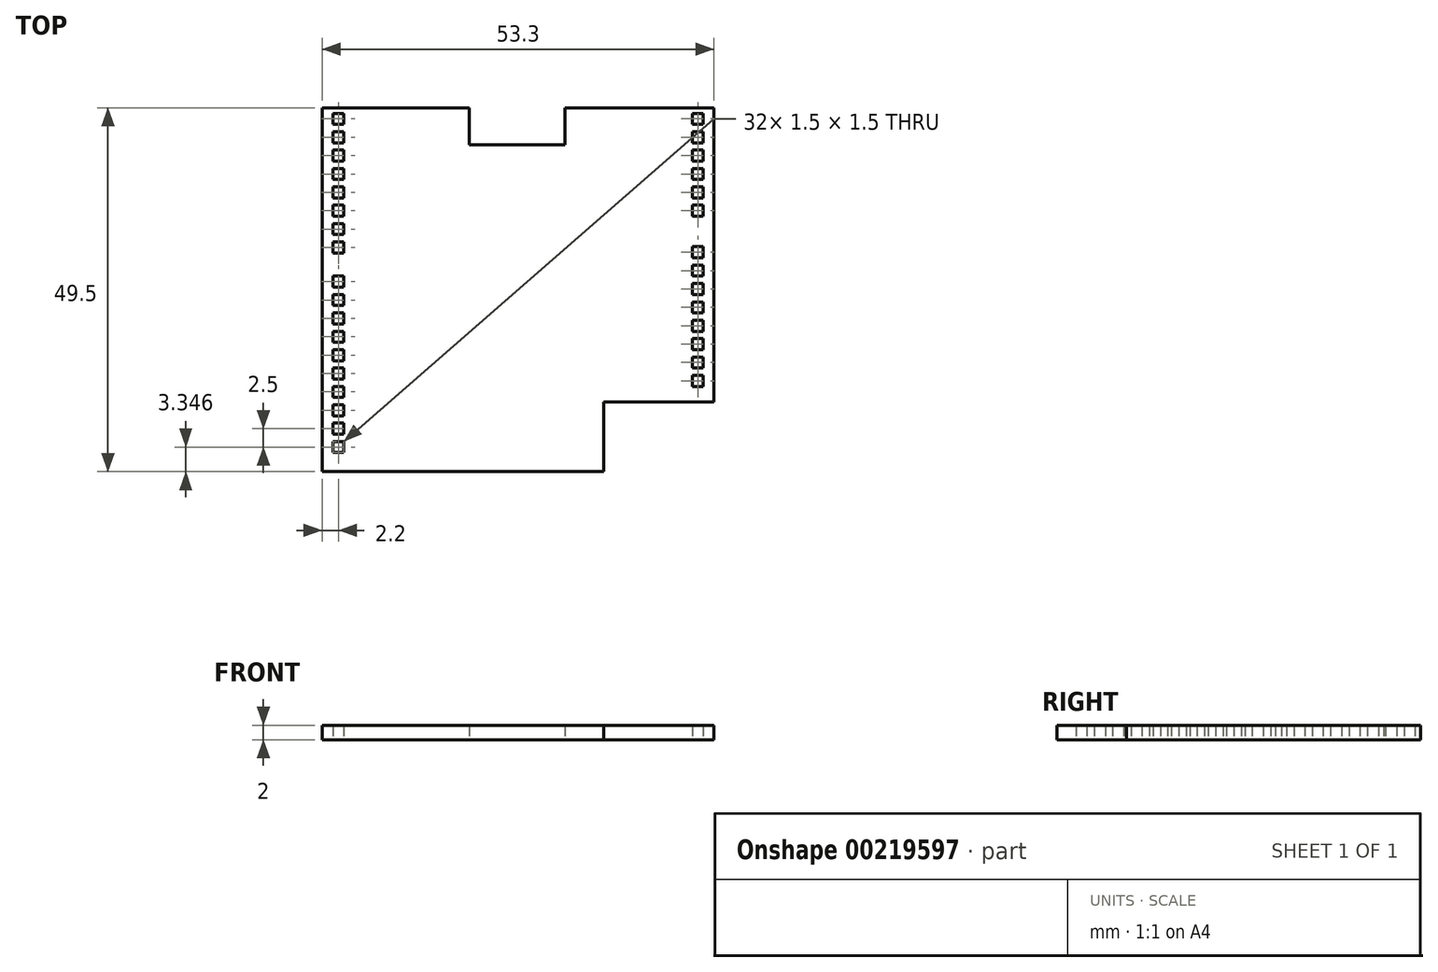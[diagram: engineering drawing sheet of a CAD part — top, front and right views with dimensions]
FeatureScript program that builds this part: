
annotation { "Feature Type Name" : "Feature", "Feature Type Description" : "" }
export const myFeature = defineFeature(function(context is Context, id is Id, definition is map)
    precondition{}
    {
        {
            var Q0;
            Q0=qCreatedBy(makeId("Top.planeOp"),FACE);
            var sketch = newSketch(context, id + "F0", { "sketchPlane" : qUnion([Q0])});
            skLineSegment(sketch, "E0.bottom", {"start": v(26.65, 29.09) * mm, "end": v(6.35, 29.09) * mm});
            skLineSegment(sketch, "E0.top", {"start": v(26.65, -29.09) * mm, "end": v(-26.65, -29.09) * mm, "construction": true});
            skLineSegment(sketch, "E0.left", {"start": v(26.65, 29.09) * mm, "end": v(26.65, -29.09) * mm});
            skLineSegment(sketch, "E0.right", {"start": v(-26.65, 29.09) * mm, "end": v(-26.65, -29.09) * mm});
            skPoint(sketch, "E0.middle", {"position": v(0, 0) * mm});
            skLineSegment(sketch, "E1.top", {"start": v(-6.65, 24.09) * mm, "end": v(6.35, 24.09) * mm});
            skLineSegment(sketch, "E1.left", {"start": v(-6.65, 29.09) * mm, "end": v(-6.65, 24.09) * mm});
            skLineSegment(sketch, "E1.right", {"start": v(6.35, 29.09) * mm, "end": v(6.35, 24.09) * mm});
            skLineSegment(sketch, "E2.bottom", {"start": v(-25.45, 29.09) * mm, "end": v(-23.45, 29.09) * mm});
            skLineSegment(sketch, "E2.top", {"start": v(-25.45, -18.91) * mm, "end": v(-23.45, -18.91) * mm, "construction": true});
            skLineSegment(sketch, "E2.left", {"start": v(-25.45, 29.09) * mm, "end": v(-25.45, 9.09) * mm, "construction": true});
            skLineSegment(sketch, "E2.right", {"start": v(-23.45, 29.09) * mm, "end": v(-23.45, 9.09) * mm, "construction": true});
            skLineSegment(sketch, "E3.bottom", {"start": v(23.45, 29.09) * mm, "end": v(25.45, 29.09) * mm});
            skLineSegment(sketch, "E3.top", {"start": v(23.45, -9.41) * mm, "end": v(25.45, -9.41) * mm, "construction": true});
            skLineSegment(sketch, "E3.left", {"start": v(23.45, 29.09) * mm, "end": v(23.45, 13.59) * mm, "construction": true});
            skLineSegment(sketch, "E3.right", {"start": v(25.45, 29.09) * mm, "end": v(25.45, 13.59) * mm, "construction": true});
            skLineSegment(sketch, "E4.bottom", {"start": v(-23.7, 26.84) * mm, "end": v(-25.2, 26.84) * mm});
            skLineSegment(sketch, "E4.top", {"start": v(-23.7, 28.34) * mm, "end": v(-25.2, 28.34) * mm});
            skLineSegment(sketch, "E4.left", {"start": v(-23.7, 26.84) * mm, "end": v(-23.7, 28.34) * mm});
            skLineSegment(sketch, "E4.right", {"start": v(-25.2, 26.84) * mm, "end": v(-25.2, 28.34) * mm});
            skPoint(sketch, "E4.middle", {"position": v(-24.45, 27.59) * mm});
            skPoint(sketch, "E4.middle.positionSnap0", {"position": v(-24.45, 29.09) * mm});
            skPoint(sketch, "E4.centerSnap0", {"position": v(-24.45, 29.09) * mm});
            skLineSegment(sketch, "E5.left", {"start": v(25.2, 26.59) * mm, "end": v(25.2, 28.09) * mm});
            skPoint(sketch, "E5.middle", {"position": v(24.45, 27.34) * mm});
            skPoint(sketch, "E5.middle.positionSnap0", {"position": v(24.45, 29.09) * mm});
            skPoint(sketch, "E5.centerSnap0", {"position": v(24.45, 29.09) * mm});
            skPoint(sketch, "E6", {"position": v(-9.25, 35.02) * mm});
            skPoint(sketch, "E7", {"position": v(18.65, 35.02) * mm});
            skLineSegment(sketch, "E8.trimOffspring", {"start": v(-6.65, 29.09) * mm, "end": v(-26.65, 29.09) * mm});
            skLineSegment(sketch, "E9", {"start": v(-26.65, -20.41) * mm, "end": v(11.65, -20.41) * mm});
            skLineSegment(sketch, "E10", {"start": v(11.65, -20.41) * mm, "end": v(11.65, -10.91) * mm});
            skLineSegment(sketch, "E11", {"start": v(11.65, -10.91) * mm, "end": v(26.65, -10.91) * mm});
            skLineSegment(sketch, "E12", {"start": v(-25.45, 9.09) * mm, "end": v(-23.45, 9.09) * mm, "construction": true});
            skLineSegment(sketch, "E13", {"start": v(-23.45, 7.09) * mm, "end": v(-25.45, 7.09) * mm, "construction": true});
            skLineSegment(sketch, "E14.trimOffspring", {"start": v(-23.45, 7.09) * mm, "end": v(-23.45, -18.91) * mm, "construction": true});
            skLineSegment(sketch, "E15.trimOffspring", {"start": v(-25.45, 7.09) * mm, "end": v(-25.45, -18.91) * mm, "construction": true});
            skLineSegment(sketch, "E16", {"start": v(23.45, 13.59) * mm, "end": v(25.45, 13.59) * mm, "construction": true});
            skLineSegment(sketch, "E17", {"start": v(25.45, 11.09) * mm, "end": v(23.45, 11.09) * mm, "construction": true});
            skLineSegment(sketch, "E18.trimOffspring", {"start": v(23.45, 11.09) * mm, "end": v(23.45, -9.41) * mm, "construction": true});
            skLineSegment(sketch, "E19.trimOffspring", {"start": v(25.45, 11.09) * mm, "end": v(25.45, -9.41) * mm, "construction": true});
            skLineSegment(sketch, "E20.0.1.0", {"start": v(-23.7, 24.34) * mm, "end": v(-23.7, 25.84) * mm});
            skPoint(sketch, "E20.0.1.1", {"position": v(-24.45, 25.09) * mm});
            skLineSegment(sketch, "E20.0.1.2", {"start": v(-23.7, 25.84) * mm, "end": v(-25.2, 25.84) * mm});
            skLineSegment(sketch, "E20.0.1.3", {"start": v(-23.7, 24.34) * mm, "end": v(-25.2, 24.34) * mm});
            skLineSegment(sketch, "E20.0.1.4", {"start": v(-25.2, 24.34) * mm, "end": v(-25.2, 25.84) * mm});
            skLineSegment(sketch, "E20.0.2.0", {"start": v(-23.7, 21.84) * mm, "end": v(-23.7, 23.34) * mm});
            skPoint(sketch, "E20.0.2.1", {"position": v(-24.45, 22.59) * mm});
            skLineSegment(sketch, "E20.0.2.2", {"start": v(-23.7, 23.34) * mm, "end": v(-25.2, 23.34) * mm});
            skLineSegment(sketch, "E20.0.2.3", {"start": v(-23.7, 21.84) * mm, "end": v(-25.2, 21.84) * mm});
            skLineSegment(sketch, "E20.0.2.4", {"start": v(-25.2, 21.84) * mm, "end": v(-25.2, 23.34) * mm});
            skLineSegment(sketch, "E20.0.3.0", {"start": v(-23.7, 19.34) * mm, "end": v(-23.7, 20.84) * mm});
            skPoint(sketch, "E20.0.3.1", {"position": v(-24.45, 20.09) * mm});
            skLineSegment(sketch, "E20.0.3.2", {"start": v(-23.7, 20.84) * mm, "end": v(-25.2, 20.84) * mm});
            skLineSegment(sketch, "E20.0.3.3", {"start": v(-23.7, 19.34) * mm, "end": v(-25.2, 19.34) * mm});
            skLineSegment(sketch, "E20.0.3.4", {"start": v(-25.2, 19.34) * mm, "end": v(-25.2, 20.84) * mm});
            skLineSegment(sketch, "E20.0.4.0", {"start": v(-23.7, 16.84) * mm, "end": v(-23.7, 18.34) * mm});
            skPoint(sketch, "E20.0.4.1", {"position": v(-24.45, 17.59) * mm});
            skLineSegment(sketch, "E20.0.4.2", {"start": v(-23.7, 18.34) * mm, "end": v(-25.2, 18.34) * mm});
            skLineSegment(sketch, "E20.0.4.3", {"start": v(-23.7, 16.84) * mm, "end": v(-25.2, 16.84) * mm});
            skLineSegment(sketch, "E20.0.4.4", {"start": v(-25.2, 16.84) * mm, "end": v(-25.2, 18.34) * mm});
            skLineSegment(sketch, "E20.0.5.0", {"start": v(-23.7, 14.34) * mm, "end": v(-23.7, 15.84) * mm});
            skPoint(sketch, "E20.0.5.1", {"position": v(-24.45, 15.09) * mm});
            skLineSegment(sketch, "E20.0.5.2", {"start": v(-23.7, 15.84) * mm, "end": v(-25.2, 15.84) * mm});
            skLineSegment(sketch, "E20.0.5.3", {"start": v(-23.7, 14.34) * mm, "end": v(-25.2, 14.34) * mm});
            skLineSegment(sketch, "E20.0.5.4", {"start": v(-25.2, 14.34) * mm, "end": v(-25.2, 15.84) * mm});
            skLineSegment(sketch, "E20.0.6.0", {"start": v(-23.7, 11.84) * mm, "end": v(-23.7, 13.34) * mm});
            skPoint(sketch, "E20.0.6.1", {"position": v(-24.45, 12.59) * mm});
            skLineSegment(sketch, "E20.0.6.2", {"start": v(-23.7, 13.34) * mm, "end": v(-25.2, 13.34) * mm});
            skLineSegment(sketch, "E20.0.6.3", {"start": v(-23.7, 11.84) * mm, "end": v(-25.2, 11.84) * mm});
            skLineSegment(sketch, "E20.0.6.4", {"start": v(-25.2, 11.84) * mm, "end": v(-25.2, 13.34) * mm});
            skLineSegment(sketch, "E20.0.7.0", {"start": v(-23.7, 9.34) * mm, "end": v(-23.7, 10.84) * mm});
            skPoint(sketch, "E20.0.7.1", {"position": v(-24.45, 10.09) * mm});
            skLineSegment(sketch, "E20.0.7.2", {"start": v(-23.7, 10.84) * mm, "end": v(-25.2, 10.84) * mm});
            skLineSegment(sketch, "E20.0.7.3", {"start": v(-23.7, 9.34) * mm, "end": v(-25.2, 9.34) * mm});
            skLineSegment(sketch, "E20.0.7.4", {"start": v(-25.2, 9.34) * mm, "end": v(-25.2, 10.84) * mm});
            skLineSegment(sketch, "E20.direction1", {"start": v(-25.2, 26.84) * mm, "end": v(-0.2, 26.84) * mm, "construction": true});
            skLineSegment(sketch, "E20.direction2", {"start": v(-25.2, 26.84) * mm, "end": v(-25.2, 24.34) * mm, "construction": true});
            skLineSegment(sketch, "E21.bottom", {"start": v(-23.7, 4.69) * mm, "end": v(-25.2, 4.69) * mm});
            skLineSegment(sketch, "E21.top", {"start": v(-23.7, 6.19) * mm, "end": v(-25.2, 6.19) * mm});
            skLineSegment(sketch, "E21.left", {"start": v(-23.7, 4.69) * mm, "end": v(-23.7, 6.19) * mm});
            skLineSegment(sketch, "E21.right", {"start": v(-25.2, 4.69) * mm, "end": v(-25.2, 6.19) * mm});
            skPoint(sketch, "E21.middle", {"position": v(-24.45, 5.44) * mm});
            skPoint(sketch, "E21.middle.positionSnap0", {"position": v(-24.45, 7.09) * mm});
            skPoint(sketch, "E21.centerSnap0", {"position": v(-24.45, 7.09) * mm});
            skLineSegment(sketch, "E22.0.1.0", {"start": v(-25.2, 2.19) * mm, "end": v(-25.2, 3.69) * mm});
            skPoint(sketch, "E22.0.1.1", {"position": v(-24.45, 2.94) * mm});
            skLineSegment(sketch, "E22.0.1.2", {"start": v(-23.7, 2.19) * mm, "end": v(-23.7, 3.69) * mm});
            skLineSegment(sketch, "E22.0.1.3", {"start": v(-23.7, 2.19) * mm, "end": v(-25.2, 2.19) * mm});
            skLineSegment(sketch, "E22.0.1.4", {"start": v(-23.7, 3.69) * mm, "end": v(-25.2, 3.69) * mm});
            skLineSegment(sketch, "E22.0.2.0", {"start": v(-25.2, -0.31) * mm, "end": v(-25.2, 1.19) * mm});
            skPoint(sketch, "E22.0.2.1", {"position": v(-24.45, 0.44) * mm});
            skLineSegment(sketch, "E22.0.2.2", {"start": v(-23.7, -0.31) * mm, "end": v(-23.7, 1.19) * mm});
            skLineSegment(sketch, "E22.0.2.3", {"start": v(-23.7, -0.31) * mm, "end": v(-25.2, -0.31) * mm});
            skLineSegment(sketch, "E22.0.2.4", {"start": v(-23.7, 1.19) * mm, "end": v(-25.2, 1.19) * mm});
            skLineSegment(sketch, "E22.0.3.0", {"start": v(-25.2, -2.81) * mm, "end": v(-25.2, -1.31) * mm});
            skPoint(sketch, "E22.0.3.1", {"position": v(-24.45, -2.06) * mm});
            skLineSegment(sketch, "E22.0.3.2", {"start": v(-23.7, -2.81) * mm, "end": v(-23.7, -1.31) * mm});
            skLineSegment(sketch, "E22.0.3.3", {"start": v(-23.7, -2.81) * mm, "end": v(-25.2, -2.81) * mm});
            skLineSegment(sketch, "E22.0.3.4", {"start": v(-23.7, -1.31) * mm, "end": v(-25.2, -1.31) * mm});
            skLineSegment(sketch, "E22.0.4.0", {"start": v(-25.2, -5.31) * mm, "end": v(-25.2, -3.81) * mm});
            skPoint(sketch, "E22.0.4.1", {"position": v(-24.45, -4.56) * mm});
            skLineSegment(sketch, "E22.0.4.2", {"start": v(-23.7, -5.31) * mm, "end": v(-23.7, -3.81) * mm});
            skLineSegment(sketch, "E22.0.4.3", {"start": v(-23.7, -5.31) * mm, "end": v(-25.2, -5.31) * mm});
            skLineSegment(sketch, "E22.0.4.4", {"start": v(-23.7, -3.81) * mm, "end": v(-25.2, -3.81) * mm});
            skLineSegment(sketch, "E22.0.5.0", {"start": v(-25.2, -7.81) * mm, "end": v(-25.2, -6.31) * mm});
            skPoint(sketch, "E22.0.5.1", {"position": v(-24.45, -7.06) * mm});
            skLineSegment(sketch, "E22.0.5.2", {"start": v(-23.7, -7.81) * mm, "end": v(-23.7, -6.31) * mm});
            skLineSegment(sketch, "E22.0.5.3", {"start": v(-23.7, -7.81) * mm, "end": v(-25.2, -7.81) * mm});
            skLineSegment(sketch, "E22.0.5.4", {"start": v(-23.7, -6.31) * mm, "end": v(-25.2, -6.31) * mm});
            skLineSegment(sketch, "E22.0.6.0", {"start": v(-25.2, -10.31) * mm, "end": v(-25.2, -8.81) * mm});
            skPoint(sketch, "E22.0.6.1", {"position": v(-24.45, -9.56) * mm});
            skLineSegment(sketch, "E22.0.6.2", {"start": v(-23.7, -10.31) * mm, "end": v(-23.7, -8.81) * mm});
            skLineSegment(sketch, "E22.0.6.3", {"start": v(-23.7, -10.31) * mm, "end": v(-25.2, -10.31) * mm});
            skLineSegment(sketch, "E22.0.6.4", {"start": v(-23.7, -8.81) * mm, "end": v(-25.2, -8.81) * mm});
            skLineSegment(sketch, "E22.0.7.0", {"start": v(-25.2, -12.81) * mm, "end": v(-25.2, -11.31) * mm});
            skPoint(sketch, "E22.0.7.1", {"position": v(-24.45, -12.06) * mm});
            skLineSegment(sketch, "E22.0.7.2", {"start": v(-23.7, -12.81) * mm, "end": v(-23.7, -11.31) * mm});
            skLineSegment(sketch, "E22.0.7.3", {"start": v(-23.7, -12.81) * mm, "end": v(-25.2, -12.81) * mm});
            skLineSegment(sketch, "E22.0.7.4", {"start": v(-23.7, -11.31) * mm, "end": v(-25.2, -11.31) * mm});
            skLineSegment(sketch, "E22.0.8.0", {"start": v(-25.2, -15.31) * mm, "end": v(-25.2, -13.81) * mm});
            skPoint(sketch, "E22.0.8.1", {"position": v(-24.45, -14.56) * mm});
            skLineSegment(sketch, "E22.0.8.2", {"start": v(-23.7, -15.31) * mm, "end": v(-23.7, -13.81) * mm});
            skLineSegment(sketch, "E22.0.8.3", {"start": v(-23.7, -15.31) * mm, "end": v(-25.2, -15.31) * mm});
            skLineSegment(sketch, "E22.0.8.4", {"start": v(-23.7, -13.81) * mm, "end": v(-25.2, -13.81) * mm});
            skLineSegment(sketch, "E22.0.9.0", {"start": v(-25.2, -17.81) * mm, "end": v(-25.2, -16.31) * mm});
            skPoint(sketch, "E22.0.9.1", {"position": v(-24.45, -17.06) * mm});
            skLineSegment(sketch, "E22.0.9.2", {"start": v(-23.7, -17.81) * mm, "end": v(-23.7, -16.31) * mm});
            skLineSegment(sketch, "E22.0.9.3", {"start": v(-23.7, -17.81) * mm, "end": v(-25.2, -17.81) * mm});
            skLineSegment(sketch, "E22.0.9.4", {"start": v(-23.7, -16.31) * mm, "end": v(-25.2, -16.31) * mm});
            skLineSegment(sketch, "E22.direction1", {"start": v(-25.2, 4.69) * mm, "end": v(-0.2, 4.69) * mm, "construction": true});
            skLineSegment(sketch, "E22.direction2", {"start": v(-25.2, 4.69) * mm, "end": v(-25.2, 2.19) * mm, "construction": true});
            skLineSegment(sketch, "E23", {"start": v(0, 35.6) * mm, "end": v(0, -47.35) * mm, "construction": true});
            skLineSegment(sketch, "E24.MirrorCS", {"start": v(25.2, 24.34) * mm, "end": v(25.2, 25.84) * mm});
            skPoint(sketch, "E25.MirrorP", {"position": v(24.45, 27.59) * mm});
            skPoint(sketch, "E26.MirrorP", {"position": v(24.45, 20.09) * mm});
            skLineSegment(sketch, "E27.MirrorCS", {"start": v(25.2, 21.84) * mm, "end": v(25.2, 23.34) * mm});
            skLineSegment(sketch, "E28.MirrorCS", {"start": v(23.7, 14.34) * mm, "end": v(23.7, 15.84) * mm});
            skLineSegment(sketch, "E29.MirrorCS", {"start": v(23.7, 24.34) * mm, "end": v(23.7, 25.84) * mm});
            skPoint(sketch, "E30.MirrorP", {"position": v(24.45, 17.59) * mm});
            skLineSegment(sketch, "E31.MirrorCS", {"start": v(23.7, 19.34) * mm, "end": v(23.7, 20.84) * mm});
            skLineSegment(sketch, "E32.MirrorCS", {"start": v(23.7, 15.84) * mm, "end": v(25.2, 15.84) * mm});
            skLineSegment(sketch, "E33.MirrorCS", {"start": v(23.7, 19.34) * mm, "end": v(25.2, 19.34) * mm});
            skLineSegment(sketch, "E34.MirrorCS", {"start": v(23.7, 25.84) * mm, "end": v(25.2, 25.84) * mm});
            skPoint(sketch, "E35.MirrorP", {"position": v(24.45, 15.09) * mm});
            skLineSegment(sketch, "E36.MirrorCS", {"start": v(25.2, 16.84) * mm, "end": v(25.2, 18.34) * mm});
            skLineSegment(sketch, "E37.MirrorCS", {"start": v(25.2, 26.84) * mm, "end": v(25.2, 28.34) * mm});
            skPoint(sketch, "E38.MirrorP", {"position": v(24.45, 22.59) * mm});
            skLineSegment(sketch, "E39.MirrorCS", {"start": v(23.7, 21.84) * mm, "end": v(25.2, 21.84) * mm});
            skLineSegment(sketch, "E40.MirrorCS", {"start": v(23.7, 16.84) * mm, "end": v(25.2, 16.84) * mm});
            skLineSegment(sketch, "E41.MirrorCS", {"start": v(23.7, 26.84) * mm, "end": v(23.7, 28.34) * mm});
            skPoint(sketch, "E42.MirrorP", {"position": v(24.45, 25.09) * mm});
            skLineSegment(sketch, "E43.MirrorCS", {"start": v(23.7, 23.34) * mm, "end": v(25.2, 23.34) * mm});
            skLineSegment(sketch, "E44.MirrorCS", {"start": v(25.2, 26.84) * mm, "end": v(25.2, 24.34) * mm, "construction": true});
            skLineSegment(sketch, "E45.MirrorCS", {"start": v(23.7, 18.34) * mm, "end": v(25.2, 18.34) * mm});
            skLineSegment(sketch, "E46.MirrorCS", {"start": v(23.7, 28.34) * mm, "end": v(25.2, 28.34) * mm});
            skLineSegment(sketch, "E47.MirrorCS", {"start": v(23.7, 21.84) * mm, "end": v(23.7, 23.34) * mm});
            skLineSegment(sketch, "E48.MirrorCS", {"start": v(23.7, 20.84) * mm, "end": v(25.2, 20.84) * mm});
            skLineSegment(sketch, "E49.MirrorCS", {"start": v(23.7, 26.84) * mm, "end": v(25.2, 26.84) * mm});
            skLineSegment(sketch, "E50.MirrorCS", {"start": v(25.2, 14.34) * mm, "end": v(25.2, 15.84) * mm});
            skLineSegment(sketch, "E51.MirrorCS", {"start": v(23.7, 16.84) * mm, "end": v(23.7, 18.34) * mm});
            skLineSegment(sketch, "E52.MirrorCS", {"start": v(23.7, 14.34) * mm, "end": v(25.2, 14.34) * mm});
            skLineSegment(sketch, "E53.MirrorCS", {"start": v(23.7, 24.34) * mm, "end": v(25.2, 24.34) * mm});
            skLineSegment(sketch, "E54.MirrorCS", {"start": v(25.2, 19.34) * mm, "end": v(25.2, 20.84) * mm});
            skLineSegment(sketch, "E55.bottom", {"start": v(25.2, 8.69) * mm, "end": v(23.7, 8.69) * mm});
            skLineSegment(sketch, "E55.top", {"start": v(25.2, 10.19) * mm, "end": v(23.7, 10.19) * mm});
            skLineSegment(sketch, "E55.left", {"start": v(25.2, 8.69) * mm, "end": v(25.2, 10.19) * mm});
            skLineSegment(sketch, "E55.right", {"start": v(23.7, 8.69) * mm, "end": v(23.7, 10.19) * mm});
            skPoint(sketch, "E55.middle", {"position": v(24.45, 9.44) * mm});
            skPoint(sketch, "E55.middle.positionSnap0", {"position": v(24.45, 11.09) * mm});
            skPoint(sketch, "E55.centerSnap0", {"position": v(24.45, 11.09) * mm});
            skLineSegment(sketch, "E56.0.1.0", {"start": v(25.2, 7.69) * mm, "end": v(23.7, 7.69) * mm});
            skLineSegment(sketch, "E56.0.1.1", {"start": v(23.7, 6.19) * mm, "end": v(23.7, 7.69) * mm});
            skLineSegment(sketch, "E56.0.1.2", {"start": v(25.2, 6.19) * mm, "end": v(25.2, 7.69) * mm});
            skLineSegment(sketch, "E56.0.1.3", {"start": v(25.2, 6.19) * mm, "end": v(23.7, 6.19) * mm});
            skPoint(sketch, "E56.0.1.4", {"position": v(24.45, 6.94) * mm});
            skLineSegment(sketch, "E56.0.2.0", {"start": v(25.2, 5.19) * mm, "end": v(23.7, 5.19) * mm});
            skLineSegment(sketch, "E56.0.2.1", {"start": v(23.7, 3.69) * mm, "end": v(23.7, 5.19) * mm});
            skLineSegment(sketch, "E56.0.2.2", {"start": v(25.2, 3.69) * mm, "end": v(25.2, 5.19) * mm});
            skLineSegment(sketch, "E56.0.2.3", {"start": v(25.2, 3.69) * mm, "end": v(23.7, 3.69) * mm});
            skPoint(sketch, "E56.0.2.4", {"position": v(24.45, 4.44) * mm});
            skLineSegment(sketch, "E56.0.3.0", {"start": v(25.2, 2.69) * mm, "end": v(23.7, 2.69) * mm});
            skLineSegment(sketch, "E56.0.3.1", {"start": v(23.7, 1.19) * mm, "end": v(23.7, 2.69) * mm});
            skLineSegment(sketch, "E56.0.3.2", {"start": v(25.2, 1.19) * mm, "end": v(25.2, 2.69) * mm});
            skLineSegment(sketch, "E56.0.3.3", {"start": v(25.2, 1.19) * mm, "end": v(23.7, 1.19) * mm});
            skPoint(sketch, "E56.0.3.4", {"position": v(24.45, 1.94) * mm});
            skLineSegment(sketch, "E56.0.4.0", {"start": v(25.2, 0.19) * mm, "end": v(23.7, 0.19) * mm});
            skLineSegment(sketch, "E56.0.4.1", {"start": v(23.7, -1.31) * mm, "end": v(23.7, 0.19) * mm});
            skLineSegment(sketch, "E56.0.4.2", {"start": v(25.2, -1.31) * mm, "end": v(25.2, 0.19) * mm});
            skLineSegment(sketch, "E56.0.4.3", {"start": v(25.2, -1.31) * mm, "end": v(23.7, -1.31) * mm});
            skPoint(sketch, "E56.0.4.4", {"position": v(24.45, -0.56) * mm});
            skLineSegment(sketch, "E56.0.5.0", {"start": v(25.2, -2.31) * mm, "end": v(23.7, -2.31) * mm});
            skLineSegment(sketch, "E56.0.5.1", {"start": v(23.7, -3.81) * mm, "end": v(23.7, -2.31) * mm});
            skLineSegment(sketch, "E56.0.5.2", {"start": v(25.2, -3.81) * mm, "end": v(25.2, -2.31) * mm});
            skLineSegment(sketch, "E56.0.5.3", {"start": v(25.2, -3.81) * mm, "end": v(23.7, -3.81) * mm});
            skPoint(sketch, "E56.0.5.4", {"position": v(24.45, -3.06) * mm});
            skLineSegment(sketch, "E56.0.6.0", {"start": v(25.2, -4.81) * mm, "end": v(23.7, -4.81) * mm});
            skLineSegment(sketch, "E56.0.6.1", {"start": v(23.7, -6.31) * mm, "end": v(23.7, -4.81) * mm});
            skLineSegment(sketch, "E56.0.6.2", {"start": v(25.2, -6.31) * mm, "end": v(25.2, -4.81) * mm});
            skLineSegment(sketch, "E56.0.6.3", {"start": v(25.2, -6.31) * mm, "end": v(23.7, -6.31) * mm});
            skPoint(sketch, "E56.0.6.4", {"position": v(24.45, -5.56) * mm});
            skLineSegment(sketch, "E56.0.7.0", {"start": v(25.2, -7.31) * mm, "end": v(23.7, -7.31) * mm});
            skLineSegment(sketch, "E56.0.7.1", {"start": v(23.7, -8.81) * mm, "end": v(23.7, -7.31) * mm});
            skLineSegment(sketch, "E56.0.7.2", {"start": v(25.2, -8.81) * mm, "end": v(25.2, -7.31) * mm});
            skLineSegment(sketch, "E56.0.7.3", {"start": v(25.2, -8.81) * mm, "end": v(23.7, -8.81) * mm});
            skPoint(sketch, "E56.0.7.4", {"position": v(24.45, -8.06) * mm});
            skLineSegment(sketch, "E56.direction1", {"start": v(23.7, 8.69) * mm, "end": v(48.7, 8.69) * mm, "construction": true});
            skLineSegment(sketch, "E56.direction2", {"start": v(23.7, 8.69) * mm, "end": v(23.7, 6.19) * mm, "construction": true});
            skSolve(sketch);
        }
        {
            var Q0;
            Q0=makeQuery(id+"F0.imprint","IMPRINT",FACE,{"disambiguationData":[TD([[makeQuery(id+"F0.imprint","IMPRINT",EDGE,{"derivedFrom":sQuery(id+"F0.wireOp",EDGE,"E1.top")}),-1.0]])]});
            extrude(context, id + "F1", {"entities" : qUnion([Q0]), "depth" : 2 * mm});
        }
    });
